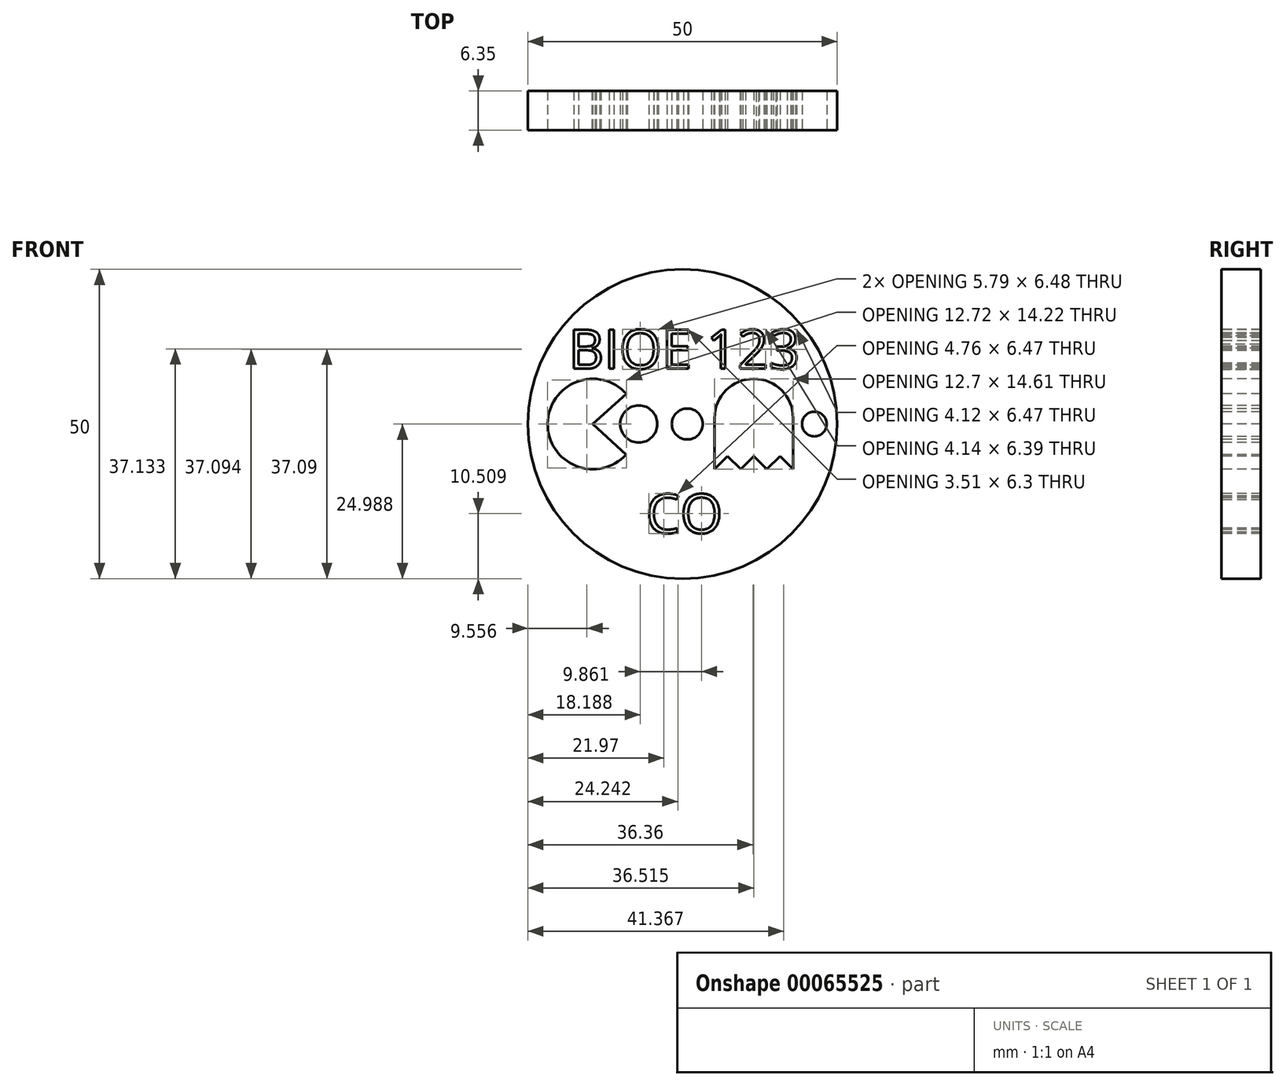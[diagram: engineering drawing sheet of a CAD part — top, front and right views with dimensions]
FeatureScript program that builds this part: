
annotation { "Feature Type Name" : "Feature", "Feature Type Description" : "" }
export const myFeature = defineFeature(function(context is Context, id is Id, definition is map)
    precondition{}
    {
        {
            var Q0;
            Q0=qCreatedBy(makeId("Front.planeOp"),FACE);
            var sketch = newSketch(context, id + "F0", { "sketchPlane" : qUnion([Q0])});
            skCircle(sketch, "E0", {"center": v(0, 0) * mm, "radius": 25 * mm});
            skSolve(sketch);
        }
        {
            var Q0;
            Q0 = qSketchRegion(id + "F0", true);
            extrude(context, id + "F1", {"entities" : qUnion([Q0]), "depth" : 6.35 * mm});
        }
        {
            var Q0;
            Q0=makeQuery(id+"F1.opExtrude","CAP_FACE",FACE,{"disambiguationData":[OSD([sQuery(id+"F0.wireOp",EDGE,"E0")])],"isStart":false});
            var sketch = newSketch(context, id + "F2", { "sketchPlane" : qUnion([Q0])});
            skText(sketch, "E1", { "text": "BIOE 123", "fontName": "OpenSans-Regular.ttf"});
            skText(sketch, "E2", { "text": "CO", "fontName": "OpenSans-Regular.ttf"});
            skArc(sketch, "E3", {"start": v(-9.08, 4.9) * mm, "mid": v(-21.8, 0.06) * mm, "end": v(-9.16, -4.97) * mm});
            skLineSegment(sketch, "E4", {"start": v(-14.5, 0) * mm, "end": v(-9.08, 4.9) * mm});
            skLineSegment(sketch, "E5", {"start": v(-9.16, -4.97) * mm, "end": v(-14.5, 0) * mm});
            skCircle(sketch, "E6", {"center": v(-7.08, 0) * mm, "radius": 3 * mm});
            skLineSegment(sketch, "E7.left", {"start": v(5.17, 0.95) * mm, "end": v(5.17, -7.3) * mm});
            skLineSegment(sketch, "E7.right", {"start": v(17.87, 0.95) * mm, "end": v(17.87, -7.3) * mm});
            skArc(sketch, "E8", {"start": v(17.87, 0.95) * mm, "mid": v(11.52, 7.3) * mm, "end": v(5.17, 0.95) * mm});
            skLineSegment(sketch, "E9", {"start": v(5.17, -7.3) * mm, "end": v(17.87, -7.3) * mm, "construction": true});
            skLineSegment(sketch, "E10", {"start": v(5.17, 0.95) * mm, "end": v(11.52, 0.95) * mm, "construction": true});
            skLineSegment(sketch, "E11", {"start": v(11.52, 0.95) * mm, "end": v(17.87, 0.95) * mm, "construction": true});
            skCircle(sketch, "E12", {"center": v(0.77, 0) * mm, "radius": 2.5 * mm});
            skCircle(sketch, "E13", {"center": v(21.3, 0) * mm, "radius": 2 * mm});
            skLineSegment(sketch, "E14", {"start": v(11.52, -5.19) * mm, "end": v(9.4, -7.3) * mm});
            skLineSegment(sketch, "E15", {"start": v(9.4, -7.3) * mm, "end": v(7.28, -5.19) * mm});
            skLineSegment(sketch, "E16", {"start": v(7.28, -5.19) * mm, "end": v(5.17, -7.3) * mm});
            skLineSegment(sketch, "E17", {"start": v(11.52, -5.19) * mm, "end": v(13.63, -7.3) * mm});
            skLineSegment(sketch, "E18", {"start": v(13.63, -7.3) * mm, "end": v(15.75, -5.19) * mm});
            skLineSegment(sketch, "E19", {"start": v(15.75, -5.19) * mm, "end": v(17.87, -7.3) * mm});
            skCircle(sketch, "E20", {"center": v(0, 0) * mm, "radius": 25 * mm, "construction": true});
            skLineSegment(sketch, "E21", {"start": v(-25, 0) * mm, "end": v(25, 0) * mm, "construction": true});
            const initialGuessF2  = {"E1": [-0.01842, 0.00894, 1, 0, 0.00635], "E2": [-0.00595, -0.01764, 1, 0, 0.00635]};
            skSetInitialGuess(sketch, initialGuessF2);
            skSolve(sketch);
        }
        {
            var Q0;
            Q0 = qSketchRegion(id + "F2", true);
            extrude(context, id + "F3", {"entities" : qUnion([Q0]), "operationType" : NewBodyOperationType.REMOVE, "oppositeDirection" : true, "depth" : 25.4 * mm});
        }
    });
